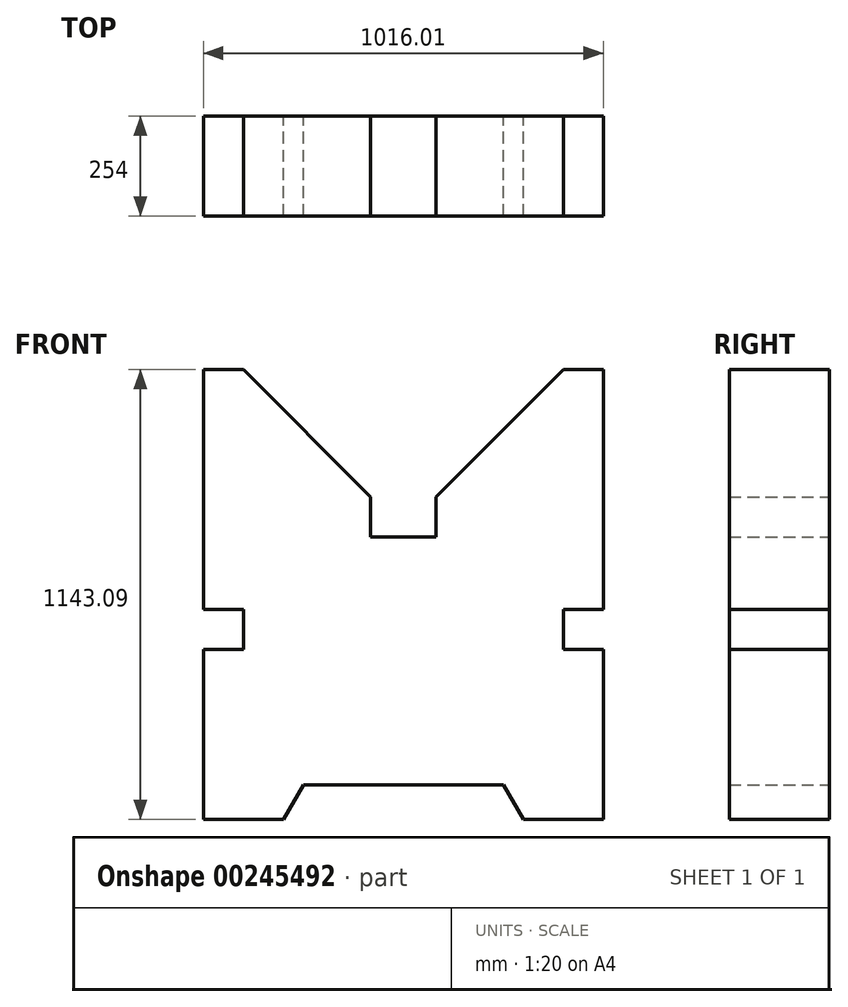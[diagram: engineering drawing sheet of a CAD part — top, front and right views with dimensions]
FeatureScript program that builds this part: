
annotation { "Feature Type Name" : "Feature", "Feature Type Description" : "" }
export const myFeature = defineFeature(function(context is Context, id is Id, definition is map)
    precondition{}
    {
        {
            var Q0;
            Q0=qCreatedBy(makeId("Front.planeOp"),FACE);
            var sketch = newSketch(context, id + "F0", { "sketchPlane" : qUnion([Q0])});
            skLineSegment(sketch, "E0", {"start": v(0, 0) * mm, "end": v(254, 0) * mm});
            skLineSegment(sketch, "E1", {"start": v(254, 0) * mm, "end": v(304.8, -87.99) * mm});
            skLineSegment(sketch, "E2", {"start": v(304.8, -87.99) * mm, "end": v(508, -87.99) * mm});
            skLineSegment(sketch, "E3", {"start": v(508, -87.99) * mm, "end": v(508, 343.81) * mm});
            skLineSegment(sketch, "E4", {"start": v(508, 343.81) * mm, "end": v(406.4, 343.81) * mm});
            skLineSegment(sketch, "E5", {"start": v(406.4, 343.81) * mm, "end": v(406.4, 445.41) * mm});
            skLineSegment(sketch, "E6", {"start": v(406.4, 445.41) * mm, "end": v(508, 445.41) * mm});
            skLineSegment(sketch, "E7", {"start": v(508, 445.41) * mm, "end": v(508, 1055.01) * mm});
            skLineSegment(sketch, "E8", {"start": v(508, 1055.01) * mm, "end": v(406.4, 1055.01) * mm});
            skLineSegment(sketch, "E9", {"start": v(406.4, 1055.01) * mm, "end": v(83.11, 731.72) * mm});
            skLineSegment(sketch, "E10", {"start": v(83.11, 731.72) * mm, "end": v(83.11, 630.12) * mm});
            skLineSegment(sketch, "E11", {"start": v(83.11, 630.12) * mm, "end": v(0.05, 630.12) * mm});
            skLineSegment(sketch, "E12", {"start": v(0.05, 630.12) * mm, "end": v(0, 0) * mm, "construction": true});
            skLineSegment(sketch, "E13.MirrorCS", {"start": v(-82.99, 731.74) * mm, "end": v(-83, 630.14) * mm});
            skLineSegment(sketch, "E14.MirrorCS", {"start": v(0, 0) * mm, "end": v(-254, 0.04) * mm});
            skLineSegment(sketch, "E15.MirrorCS", {"start": v(-254, 0.04) * mm, "end": v(-304.81, -87.94) * mm});
            skLineSegment(sketch, "E16.MirrorCS", {"start": v(-304.81, -87.94) * mm, "end": v(-508.01, -87.9) * mm});
            skLineSegment(sketch, "E17.MirrorCS", {"start": v(-83, 630.14) * mm, "end": v(0.05, 630.12) * mm});
            skLineSegment(sketch, "E18.MirrorCS", {"start": v(-507.93, 445.5) * mm, "end": v(-507.82, 1055.1) * mm});
            skLineSegment(sketch, "E19.MirrorCS", {"start": v(-508.01, -87.9) * mm, "end": v(-507.94, 343.9) * mm});
            skLineSegment(sketch, "E20.MirrorCS", {"start": v(-406.33, 445.48) * mm, "end": v(-507.93, 445.5) * mm});
            skLineSegment(sketch, "E21.MirrorCS", {"start": v(-507.82, 1055.1) * mm, "end": v(-406.22, 1055.08) * mm});
            skLineSegment(sketch, "E22.MirrorCS", {"start": v(-406.22, 1055.08) * mm, "end": v(-82.99, 731.74) * mm});
            skLineSegment(sketch, "E23.MirrorCS", {"start": v(-406.34, 343.88) * mm, "end": v(-406.33, 445.48) * mm});
            skLineSegment(sketch, "E24.MirrorCS", {"start": v(-507.94, 343.9) * mm, "end": v(-406.34, 343.88) * mm});
            skSolve(sketch);
        }
        {
            var Q0;
            Q0=makeQuery(id+"F0.imprint","IMPRINT",FACE,{"disambiguationData":[TD([[makeQuery(id+"F0.imprint","IMPRINT",EDGE,{"derivedFrom":sQuery(id+"F0.wireOp",EDGE,"E0")}),1.0]])]});
            extrude(context, id + "F1", {"entities" : qUnion([Q0]), "depth" : 254 * mm});
        }
    });
